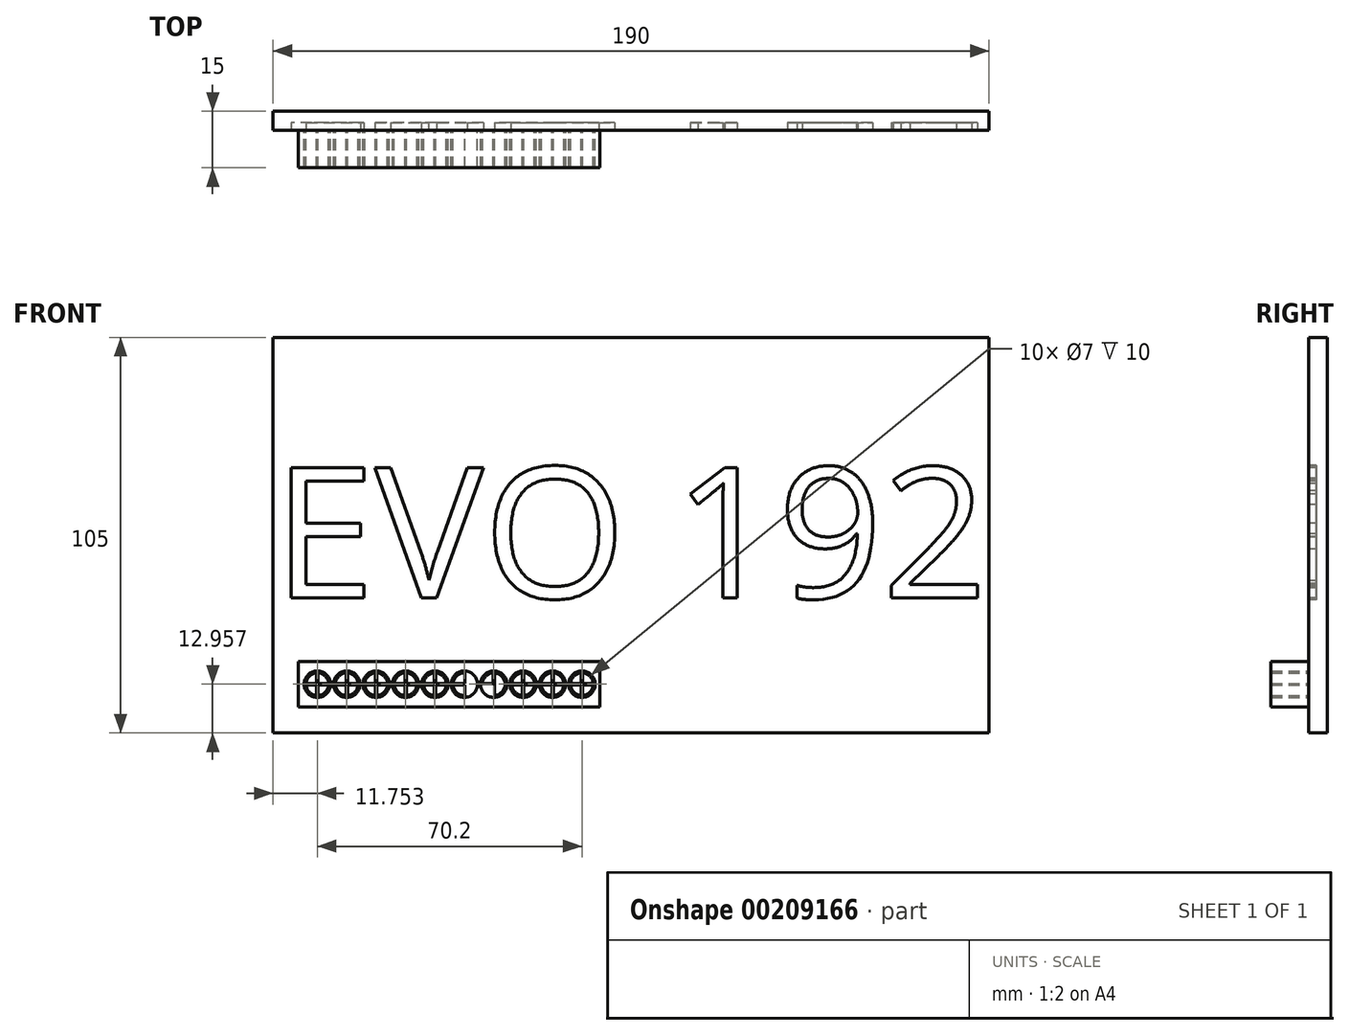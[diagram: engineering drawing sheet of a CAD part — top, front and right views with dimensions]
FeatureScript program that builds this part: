
annotation { "Feature Type Name" : "Feature", "Feature Type Description" : "" }
export const myFeature = defineFeature(function(context is Context, id is Id, definition is map)
    precondition{}
    {
        {
            var Q0;
            Q0=qCreatedBy(makeId("Front.planeOp"),FACE);
            var sketch = newSketch(context, id + "F0", { "sketchPlane" : qUnion([Q0])});
            skLineSegment(sketch, "E0.bottom", {"start": v(95, 52.5) * mm, "end": v(-95, 52.5) * mm});
            skLineSegment(sketch, "E0.top", {"start": v(95, -52.5) * mm, "end": v(-95, -52.5) * mm});
            skLineSegment(sketch, "E0.left", {"start": v(95, 52.5) * mm, "end": v(95, -52.5) * mm});
            skLineSegment(sketch, "E0.right", {"start": v(-95, 52.5) * mm, "end": v(-95, -52.5) * mm});
            skPoint(sketch, "E0.middle", {"position": v(0, 0) * mm});
            skSolve(sketch);
        }
        {
            var Q0;
            Q0 = qSketchRegion(id + "F0", true);
            extrude(context, id + "F1", {"entities" : qUnion([Q0]), "depth" : 5 * mm});
        }
        {
            var Q0;
            Q0=makeQuery(id+"F1.opExtrude","CAP_FACE",FACE,{"disambiguationData":[OSD([sQuery(id+"F0.wireOp",EDGE,"E0.bottom"),sQuery(id+"F0.wireOp",EDGE,"E0.top"),sQuery(id+"F0.wireOp",EDGE,"E0.left"),sQuery(id+"F0.wireOp",EDGE,"E0.right")])],"isStart":false});
            var sketch = newSketch(context, id + "F2", { "sketchPlane" : qUnion([Q0])});
            skText(sketch, "E1", { "text": "EVO 192", "fontName": "OpenSans-Regular.ttf"});
            const initialGuessF2  = {"E1": [-0.095, -0.01668, 1, 0, 0.03493]};
            skSetInitialGuess(sketch, initialGuessF2);
            skSolve(sketch);
        }
        {
            var Q0;
            Q0 = qSketchRegion(id + "F2", true);
            extrude(context, id + "F3", {"entities" : qUnion([Q0]), "operationType" : NewBodyOperationType.REMOVE, "oppositeDirection" : true, "depth" : 2 * mm});
        }
        {
            var Q0;
            {var subQ0=sQuery(id+"F0.wireOp",EDGE,"E0.top");var subQ1=sQuery(id+"F0.wireOp",EDGE,"E0.right");var subQ2=sQuery(id+"F0.wireOp",EDGE,"E0.bottom");var subQ3=sQuery(id+"F0.wireOp",EDGE,"E0.left");Q0=makeQuery(id+"F3.boolean.opBoolean","SPLIT",FACE,{"disambiguationData":[TD([makeQuery(id+"F1.opExtrude","SWEPT_FACE",FACE,{"disambiguationData":[OSD([subQ2])]})])],"derivedFrom":makeQuery(id+"F1.opExtrude","CAP_FACE",FACE,{"disambiguationData":[OSD([subQ2,subQ0,subQ3,subQ1])],"isStart":false})});}
            var sketch = newSketch(context, id + "F4", { "sketchPlane" : qUnion([Q0])});
            skLineSegment(sketch, "E2.bottom", {"start": v(-88.25, -33.54) * mm, "end": v(-8.25, -33.54) * mm});
            skLineSegment(sketch, "E2.top", {"start": v(-88.25, -45.54) * mm, "end": v(-8.25, -45.54) * mm});
            skLineSegment(sketch, "E2.left", {"start": v(-88.25, -33.54) * mm, "end": v(-88.25, -45.54) * mm});
            skLineSegment(sketch, "E2.right", {"start": v(-8.25, -33.54) * mm, "end": v(-8.25, -45.54) * mm});
            skCircle(sketch, "E3", {"center": v(-83.25, -39.54) * mm, "radius": 3 * mm});
            skLineSegment(sketch, "E4.0", {"start": v(-83.45, -36.54) * mm, "end": v(-83.45, -42.54) * mm});
            skLineSegment(sketch, "E5.0", {"start": v(-83.05, -36.54) * mm, "end": v(-83.05, -42.54) * mm});
            skLineSegment(sketch, "E6.0", {"start": v(-86.25, -39.74) * mm, "end": v(-80.25, -39.74) * mm});
            skLineSegment(sketch, "E7.0", {"start": v(-86.25, -39.34) * mm, "end": v(-80.25, -39.34) * mm});
            skCircle(sketch, "E8.1.0.0", {"center": v(-75.45, -39.54) * mm, "radius": 3 * mm});
            skLineSegment(sketch, "E8.1.0.1", {"start": v(-78.45, -39.34) * mm, "end": v(-72.45, -39.34) * mm});
            skLineSegment(sketch, "E8.1.0.2", {"start": v(-75.25, -36.54) * mm, "end": v(-75.25, -42.54) * mm});
            skLineSegment(sketch, "E8.1.0.3", {"start": v(-75.65, -36.54) * mm, "end": v(-75.65, -42.54) * mm});
            skLineSegment(sketch, "E8.1.0.4", {"start": v(-78.45, -39.74) * mm, "end": v(-72.45, -39.74) * mm});
            skCircle(sketch, "E8.2.0.0", {"center": v(-67.65, -39.54) * mm, "radius": 3 * mm});
            skLineSegment(sketch, "E8.2.0.1", {"start": v(-70.65, -39.34) * mm, "end": v(-64.65, -39.34) * mm});
            skLineSegment(sketch, "E8.2.0.2", {"start": v(-67.45, -36.54) * mm, "end": v(-67.45, -42.54) * mm});
            skLineSegment(sketch, "E8.2.0.3", {"start": v(-67.85, -36.54) * mm, "end": v(-67.85, -42.54) * mm});
            skLineSegment(sketch, "E8.2.0.4", {"start": v(-70.65, -39.74) * mm, "end": v(-64.65, -39.74) * mm});
            skCircle(sketch, "E8.3.0.0", {"center": v(-59.85, -39.54) * mm, "radius": 3 * mm});
            skLineSegment(sketch, "E8.3.0.1", {"start": v(-62.85, -39.34) * mm, "end": v(-56.85, -39.34) * mm});
            skLineSegment(sketch, "E8.3.0.2", {"start": v(-59.65, -36.54) * mm, "end": v(-59.65, -42.54) * mm});
            skLineSegment(sketch, "E8.3.0.3", {"start": v(-60.05, -36.54) * mm, "end": v(-60.05, -42.54) * mm});
            skLineSegment(sketch, "E8.3.0.4", {"start": v(-62.85, -39.74) * mm, "end": v(-56.85, -39.74) * mm});
            skCircle(sketch, "E8.4.0.0", {"center": v(-52.05, -39.54) * mm, "radius": 3 * mm});
            skLineSegment(sketch, "E8.4.0.1", {"start": v(-55.05, -39.34) * mm, "end": v(-49.05, -39.34) * mm});
            skLineSegment(sketch, "E8.4.0.2", {"start": v(-51.85, -36.54) * mm, "end": v(-51.85, -42.54) * mm});
            skLineSegment(sketch, "E8.4.0.3", {"start": v(-52.25, -36.54) * mm, "end": v(-52.25, -42.54) * mm});
            skLineSegment(sketch, "E8.4.0.4", {"start": v(-55.05, -39.74) * mm, "end": v(-49.05, -39.74) * mm});
            skCircle(sketch, "E8.5.0.0", {"center": v(-44.25, -39.54) * mm, "radius": 3 * mm});
            skLineSegment(sketch, "E8.5.0.1", {"start": v(-47.25, -39.34) * mm, "end": v(-41.25, -39.34) * mm});
            skLineSegment(sketch, "E8.5.0.2", {"start": v(-44.05, -36.54) * mm, "end": v(-44.05, -42.54) * mm});
            skLineSegment(sketch, "E8.5.0.3", {"start": v(-44.45, -36.54) * mm, "end": v(-44.45, -42.54) * mm});
            skLineSegment(sketch, "E8.5.0.4", {"start": v(-47.25, -39.74) * mm, "end": v(-41.25, -39.74) * mm});
            skCircle(sketch, "E8.6.0.0", {"center": v(-36.45, -39.54) * mm, "radius": 3 * mm});
            skLineSegment(sketch, "E8.6.0.1", {"start": v(-39.45, -39.34) * mm, "end": v(-33.45, -39.34) * mm});
            skLineSegment(sketch, "E8.6.0.2", {"start": v(-36.25, -36.54) * mm, "end": v(-36.25, -42.54) * mm});
            skLineSegment(sketch, "E8.6.0.3", {"start": v(-36.65, -36.54) * mm, "end": v(-36.65, -42.54) * mm});
            skLineSegment(sketch, "E8.6.0.4", {"start": v(-39.45, -39.74) * mm, "end": v(-33.45, -39.74) * mm});
            skCircle(sketch, "E8.7.0.0", {"center": v(-28.65, -39.54) * mm, "radius": 3 * mm});
            skLineSegment(sketch, "E8.7.0.1", {"start": v(-31.65, -39.34) * mm, "end": v(-25.65, -39.34) * mm});
            skLineSegment(sketch, "E8.7.0.2", {"start": v(-28.45, -36.54) * mm, "end": v(-28.45, -42.54) * mm});
            skLineSegment(sketch, "E8.7.0.3", {"start": v(-28.85, -36.54) * mm, "end": v(-28.85, -42.54) * mm});
            skLineSegment(sketch, "E8.7.0.4", {"start": v(-31.65, -39.74) * mm, "end": v(-25.65, -39.74) * mm});
            skCircle(sketch, "E8.8.0.0", {"center": v(-20.85, -39.54) * mm, "radius": 3 * mm});
            skLineSegment(sketch, "E8.8.0.1", {"start": v(-23.85, -39.34) * mm, "end": v(-17.85, -39.34) * mm});
            skLineSegment(sketch, "E8.8.0.2", {"start": v(-20.65, -36.54) * mm, "end": v(-20.65, -42.54) * mm});
            skLineSegment(sketch, "E8.8.0.3", {"start": v(-21.05, -36.54) * mm, "end": v(-21.05, -42.54) * mm});
            skLineSegment(sketch, "E8.8.0.4", {"start": v(-23.85, -39.74) * mm, "end": v(-17.85, -39.74) * mm});
            skCircle(sketch, "E8.9.0.0", {"center": v(-13.05, -39.54) * mm, "radius": 3 * mm});
            skLineSegment(sketch, "E8.9.0.1", {"start": v(-16.05, -39.34) * mm, "end": v(-10.05, -39.34) * mm});
            skLineSegment(sketch, "E8.9.0.2", {"start": v(-12.85, -36.54) * mm, "end": v(-12.85, -42.54) * mm});
            skLineSegment(sketch, "E8.9.0.3", {"start": v(-13.25, -36.54) * mm, "end": v(-13.25, -42.54) * mm});
            skLineSegment(sketch, "E8.9.0.4", {"start": v(-16.05, -39.74) * mm, "end": v(-10.05, -39.74) * mm});
            skLineSegment(sketch, "E8.direction1", {"start": v(-83.25, -39.54) * mm, "end": v(-75.45, -39.54) * mm, "construction": true});
            skCircle(sketch, "E9", {"center": v(-83.25, -39.54) * mm, "radius": 3.5 * mm});
            skCircle(sketch, "E10.1.0.0", {"center": v(-75.45, -39.54) * mm, "radius": 3.5 * mm});
            skCircle(sketch, "E10.2.0.0", {"center": v(-67.65, -39.54) * mm, "radius": 3.5 * mm});
            skCircle(sketch, "E10.3.0.0", {"center": v(-59.85, -39.54) * mm, "radius": 3.5 * mm});
            skCircle(sketch, "E10.4.0.0", {"center": v(-52.05, -39.54) * mm, "radius": 3.5 * mm});
            skCircle(sketch, "E10.5.0.0", {"center": v(-44.25, -39.54) * mm, "radius": 3.5 * mm});
            skCircle(sketch, "E10.6.0.0", {"center": v(-36.45, -39.54) * mm, "radius": 3.5 * mm});
            skCircle(sketch, "E10.7.0.0", {"center": v(-28.65, -39.54) * mm, "radius": 3.5 * mm});
            skCircle(sketch, "E10.8.0.0", {"center": v(-20.85, -39.54) * mm, "radius": 3.5 * mm});
            skCircle(sketch, "E10.9.0.0", {"center": v(-13.05, -39.54) * mm, "radius": 3.5 * mm});
            skSolve(sketch);
        }
        {
            var Q0;
            Q0 = qSketchRegion(id + "F4", true);
            var Q1;
            {var subQ0=sQuery(id+"F4.wireOp",EDGE,"E4.0");var subQ1=sQuery(id+"F4.wireOp",EDGE,"E3");var subQ2=makeQuery(id+"F4.imprint","INTERSECT",VERTEX,{"disambiguationData":[OD(0.0)],"derivedFrom":[subQ1,subQ0]});Q1=makeQuery(id+"F4.imprint","IMPRINT",FACE,{"disambiguationData":[TD([[makeQuery(id+"F4.imprint","IMPRINT",EDGE,{"disambiguationData":[TD([[subQ2,-1.0]])],"derivedFrom":subQ1}),1.0]])]});}
            var Q2;
            {var subQ0=sQuery(id+"F4.wireOp",EDGE,"E5.0");var subQ1=sQuery(id+"F4.wireOp",EDGE,"E3");var subQ2=makeQuery(id+"F4.imprint","INTERSECT",VERTEX,{"disambiguationData":[OD(0.0)],"derivedFrom":[subQ1,subQ0]});Q2=makeQuery(id+"F4.imprint","IMPRINT",FACE,{"disambiguationData":[TD([[makeQuery(id+"F4.imprint","IMPRINT",EDGE,{"disambiguationData":[TD([[subQ2,1.0]])],"derivedFrom":subQ1}),1.0]])]});}
            var Q3;
            {var subQ0=sQuery(id+"F4.wireOp",EDGE,"E5.0");var subQ1=sQuery(id+"F4.wireOp",EDGE,"E3");var subQ2=makeQuery(id+"F4.imprint","INTERSECT",VERTEX,{"disambiguationData":[OD(1.0)],"derivedFrom":[subQ1,subQ0]});Q3=makeQuery(id+"F4.imprint","IMPRINT",FACE,{"disambiguationData":[TD([[makeQuery(id+"F4.imprint","IMPRINT",EDGE,{"disambiguationData":[TD([[subQ2,-1.0]])],"derivedFrom":subQ1}),1.0]])]});}
            var Q4;
            {var subQ0=sQuery(id+"F4.wireOp",EDGE,"E6.0");var subQ1=sQuery(id+"F4.wireOp",EDGE,"E3");var subQ2=makeQuery(id+"F4.imprint","INTERSECT",VERTEX,{"disambiguationData":[OD(0.0)],"derivedFrom":[subQ1,subQ0]});Q4=makeQuery(id+"F4.imprint","IMPRINT",FACE,{"disambiguationData":[TD([[makeQuery(id+"F4.imprint","IMPRINT",EDGE,{"disambiguationData":[TD([[subQ2,-1.0]])],"derivedFrom":subQ1}),1.0]])]});}
            var Q5;
            {var subQ0=sQuery(id+"F4.wireOp",EDGE,"E8.1.0.3");var subQ1=sQuery(id+"F4.wireOp",EDGE,"E8.1.0.0");var subQ2=makeQuery(id+"F4.imprint","INTERSECT",VERTEX,{"disambiguationData":[OD(0.0)],"derivedFrom":[subQ1,subQ0]});Q5=makeQuery(id+"F4.imprint","IMPRINT",FACE,{"disambiguationData":[TD([[makeQuery(id+"F4.imprint","IMPRINT",EDGE,{"disambiguationData":[TD([[subQ2,-1.0]])],"derivedFrom":subQ1}),1.0]])]});}
            var Q6;
            {var subQ0=sQuery(id+"F4.wireOp",EDGE,"E8.1.0.2");var subQ1=sQuery(id+"F4.wireOp",EDGE,"E8.1.0.0");var subQ2=makeQuery(id+"F4.imprint","INTERSECT",VERTEX,{"disambiguationData":[OD(0.0)],"derivedFrom":[subQ1,subQ0]});Q6=makeQuery(id+"F4.imprint","IMPRINT",FACE,{"disambiguationData":[TD([[makeQuery(id+"F4.imprint","IMPRINT",EDGE,{"disambiguationData":[TD([[subQ2,1.0]])],"derivedFrom":subQ1}),1.0]])]});}
            var Q7;
            {var subQ0=sQuery(id+"F4.wireOp",EDGE,"E8.1.0.2");var subQ1=sQuery(id+"F4.wireOp",EDGE,"E8.1.0.0");var subQ2=makeQuery(id+"F4.imprint","INTERSECT",VERTEX,{"disambiguationData":[OD(1.0)],"derivedFrom":[subQ1,subQ0]});Q7=makeQuery(id+"F4.imprint","IMPRINT",FACE,{"disambiguationData":[TD([[makeQuery(id+"F4.imprint","IMPRINT",EDGE,{"disambiguationData":[TD([[subQ2,-1.0]])],"derivedFrom":subQ1}),1.0]])]});}
            var Q8;
            {var subQ0=sQuery(id+"F4.wireOp",EDGE,"E8.1.0.4");var subQ1=sQuery(id+"F4.wireOp",EDGE,"E8.1.0.0");var subQ2=makeQuery(id+"F4.imprint","INTERSECT",VERTEX,{"disambiguationData":[OD(0.0)],"derivedFrom":[subQ1,subQ0]});Q8=makeQuery(id+"F4.imprint","IMPRINT",FACE,{"disambiguationData":[TD([[makeQuery(id+"F4.imprint","IMPRINT",EDGE,{"disambiguationData":[TD([[subQ2,-1.0]])],"derivedFrom":subQ1}),1.0]])]});}
            var Q9;
            {var subQ0=sQuery(id+"F4.wireOp",EDGE,"E8.2.0.3");var subQ1=sQuery(id+"F4.wireOp",EDGE,"E8.2.0.0");var subQ2=makeQuery(id+"F4.imprint","INTERSECT",VERTEX,{"disambiguationData":[OD(0.0)],"derivedFrom":[subQ1,subQ0]});Q9=makeQuery(id+"F4.imprint","IMPRINT",FACE,{"disambiguationData":[TD([[makeQuery(id+"F4.imprint","IMPRINT",EDGE,{"disambiguationData":[TD([[subQ2,-1.0]])],"derivedFrom":subQ1}),1.0]])]});}
            var Q10;
            {var subQ0=sQuery(id+"F4.wireOp",EDGE,"E8.2.0.2");var subQ1=sQuery(id+"F4.wireOp",EDGE,"E8.2.0.0");var subQ2=makeQuery(id+"F4.imprint","INTERSECT",VERTEX,{"disambiguationData":[OD(0.0)],"derivedFrom":[subQ1,subQ0]});Q10=makeQuery(id+"F4.imprint","IMPRINT",FACE,{"disambiguationData":[TD([[makeQuery(id+"F4.imprint","IMPRINT",EDGE,{"disambiguationData":[TD([[subQ2,1.0]])],"derivedFrom":subQ1}),1.0]])]});}
            var Q11;
            {var subQ0=sQuery(id+"F4.wireOp",EDGE,"E8.2.0.2");var subQ1=sQuery(id+"F4.wireOp",EDGE,"E8.2.0.0");var subQ2=makeQuery(id+"F4.imprint","INTERSECT",VERTEX,{"disambiguationData":[OD(1.0)],"derivedFrom":[subQ1,subQ0]});Q11=makeQuery(id+"F4.imprint","IMPRINT",FACE,{"disambiguationData":[TD([[makeQuery(id+"F4.imprint","IMPRINT",EDGE,{"disambiguationData":[TD([[subQ2,-1.0]])],"derivedFrom":subQ1}),1.0]])]});}
            var Q12;
            {var subQ0=sQuery(id+"F4.wireOp",EDGE,"E8.2.0.4");var subQ1=sQuery(id+"F4.wireOp",EDGE,"E8.2.0.0");var subQ2=makeQuery(id+"F4.imprint","INTERSECT",VERTEX,{"disambiguationData":[OD(0.0)],"derivedFrom":[subQ1,subQ0]});Q12=makeQuery(id+"F4.imprint","IMPRINT",FACE,{"disambiguationData":[TD([[makeQuery(id+"F4.imprint","IMPRINT",EDGE,{"disambiguationData":[TD([[subQ2,-1.0]])],"derivedFrom":subQ1}),1.0]])]});}
            var Q13;
            {var subQ0=sQuery(id+"F4.wireOp",EDGE,"E8.3.0.3");var subQ1=sQuery(id+"F4.wireOp",EDGE,"E8.3.0.0");var subQ2=makeQuery(id+"F4.imprint","INTERSECT",VERTEX,{"disambiguationData":[OD(0.0)],"derivedFrom":[subQ1,subQ0]});Q13=makeQuery(id+"F4.imprint","IMPRINT",FACE,{"disambiguationData":[TD([[makeQuery(id+"F4.imprint","IMPRINT",EDGE,{"disambiguationData":[TD([[subQ2,-1.0]])],"derivedFrom":subQ1}),1.0]])]});}
            var Q14;
            {var subQ0=sQuery(id+"F4.wireOp",EDGE,"E8.3.0.2");var subQ1=sQuery(id+"F4.wireOp",EDGE,"E8.3.0.0");var subQ2=makeQuery(id+"F4.imprint","INTERSECT",VERTEX,{"disambiguationData":[OD(0.0)],"derivedFrom":[subQ1,subQ0]});Q14=makeQuery(id+"F4.imprint","IMPRINT",FACE,{"disambiguationData":[TD([[makeQuery(id+"F4.imprint","IMPRINT",EDGE,{"disambiguationData":[TD([[subQ2,1.0]])],"derivedFrom":subQ1}),1.0]])]});}
            var Q15;
            {var subQ0=sQuery(id+"F4.wireOp",EDGE,"E8.3.0.2");var subQ1=sQuery(id+"F4.wireOp",EDGE,"E8.3.0.0");var subQ2=makeQuery(id+"F4.imprint","INTERSECT",VERTEX,{"disambiguationData":[OD(1.0)],"derivedFrom":[subQ1,subQ0]});Q15=makeQuery(id+"F4.imprint","IMPRINT",FACE,{"disambiguationData":[TD([[makeQuery(id+"F4.imprint","IMPRINT",EDGE,{"disambiguationData":[TD([[subQ2,-1.0]])],"derivedFrom":subQ1}),1.0]])]});}
            var Q16;
            {var subQ0=sQuery(id+"F4.wireOp",EDGE,"E8.3.0.4");var subQ1=sQuery(id+"F4.wireOp",EDGE,"E8.3.0.0");var subQ2=makeQuery(id+"F4.imprint","INTERSECT",VERTEX,{"disambiguationData":[OD(0.0)],"derivedFrom":[subQ1,subQ0]});Q16=makeQuery(id+"F4.imprint","IMPRINT",FACE,{"disambiguationData":[TD([[makeQuery(id+"F4.imprint","IMPRINT",EDGE,{"disambiguationData":[TD([[subQ2,-1.0]])],"derivedFrom":subQ1}),1.0]])]});}
            var Q17;
            {var subQ0=sQuery(id+"F4.wireOp",EDGE,"E8.4.0.3");var subQ1=sQuery(id+"F4.wireOp",EDGE,"E8.4.0.0");var subQ2=makeQuery(id+"F4.imprint","INTERSECT",VERTEX,{"disambiguationData":[OD(0.0)],"derivedFrom":[subQ1,subQ0]});Q17=makeQuery(id+"F4.imprint","IMPRINT",FACE,{"disambiguationData":[TD([[makeQuery(id+"F4.imprint","IMPRINT",EDGE,{"disambiguationData":[TD([[subQ2,-1.0]])],"derivedFrom":subQ1}),1.0]])]});}
            var Q18;
            {var subQ0=sQuery(id+"F4.wireOp",EDGE,"E8.4.0.2");var subQ1=sQuery(id+"F4.wireOp",EDGE,"E8.4.0.0");var subQ2=makeQuery(id+"F4.imprint","INTERSECT",VERTEX,{"disambiguationData":[OD(0.0)],"derivedFrom":[subQ1,subQ0]});Q18=makeQuery(id+"F4.imprint","IMPRINT",FACE,{"disambiguationData":[TD([[makeQuery(id+"F4.imprint","IMPRINT",EDGE,{"disambiguationData":[TD([[subQ2,1.0]])],"derivedFrom":subQ1}),1.0]])]});}
            var Q19;
            {var subQ0=sQuery(id+"F4.wireOp",EDGE,"E8.4.0.2");var subQ1=sQuery(id+"F4.wireOp",EDGE,"E8.4.0.0");var subQ2=makeQuery(id+"F4.imprint","INTERSECT",VERTEX,{"disambiguationData":[OD(1.0)],"derivedFrom":[subQ1,subQ0]});Q19=makeQuery(id+"F4.imprint","IMPRINT",FACE,{"disambiguationData":[TD([[makeQuery(id+"F4.imprint","IMPRINT",EDGE,{"disambiguationData":[TD([[subQ2,-1.0]])],"derivedFrom":subQ1}),1.0]])]});}
            var Q20;
            {var subQ0=sQuery(id+"F4.wireOp",EDGE,"E8.4.0.4");var subQ1=sQuery(id+"F4.wireOp",EDGE,"E8.4.0.0");var subQ2=makeQuery(id+"F4.imprint","INTERSECT",VERTEX,{"disambiguationData":[OD(0.0)],"derivedFrom":[subQ1,subQ0]});Q20=makeQuery(id+"F4.imprint","IMPRINT",FACE,{"disambiguationData":[TD([[makeQuery(id+"F4.imprint","IMPRINT",EDGE,{"disambiguationData":[TD([[subQ2,-1.0]])],"derivedFrom":subQ1}),1.0]])]});}
            var Q21;
            {var subQ0=sQuery(id+"F4.wireOp",EDGE,"E8.5.0.3");var subQ1=sQuery(id+"F4.wireOp",EDGE,"E8.5.0.0");var subQ2=makeQuery(id+"F4.imprint","INTERSECT",VERTEX,{"disambiguationData":[OD(0.0)],"derivedFrom":[subQ1,subQ0]});Q21=makeQuery(id+"F4.imprint","IMPRINT",FACE,{"disambiguationData":[TD([[makeQuery(id+"F4.imprint","IMPRINT",EDGE,{"disambiguationData":[TD([[subQ2,-1.0]])],"derivedFrom":subQ1}),1.0]])]});}
            var Q22;
            {var subQ0=sQuery(id+"F4.wireOp",EDGE,"E8.5.0.2");var subQ1=sQuery(id+"F4.wireOp",EDGE,"E8.5.0.0");var subQ2=makeQuery(id+"F4.imprint","INTERSECT",VERTEX,{"disambiguationData":[OD(0.0)],"derivedFrom":[subQ1,subQ0]});Q22=makeQuery(id+"F4.imprint","IMPRINT",FACE,{"disambiguationData":[TD([[makeQuery(id+"F4.imprint","IMPRINT",EDGE,{"disambiguationData":[TD([[subQ2,1.0]])],"derivedFrom":subQ1}),1.0]])]});}
            var Q23;
            {var subQ0=sQuery(id+"F4.wireOp",EDGE,"E8.5.0.2");var subQ1=sQuery(id+"F4.wireOp",EDGE,"E8.5.0.0");var subQ2=makeQuery(id+"F4.imprint","INTERSECT",VERTEX,{"disambiguationData":[OD(1.0)],"derivedFrom":[subQ1,subQ0]});Q23=makeQuery(id+"F4.imprint","IMPRINT",FACE,{"disambiguationData":[TD([[makeQuery(id+"F4.imprint","IMPRINT",EDGE,{"disambiguationData":[TD([[subQ2,-1.0]])],"derivedFrom":subQ1}),1.0]])]});}
            var Q24;
            {var subQ0=sQuery(id+"F4.wireOp",EDGE,"E8.5.0.4");var subQ1=sQuery(id+"F4.wireOp",EDGE,"E8.5.0.0");var subQ2=makeQuery(id+"F4.imprint","INTERSECT",VERTEX,{"disambiguationData":[OD(0.0)],"derivedFrom":[subQ1,subQ0]});Q24=makeQuery(id+"F4.imprint","IMPRINT",FACE,{"disambiguationData":[TD([[makeQuery(id+"F4.imprint","IMPRINT",EDGE,{"disambiguationData":[TD([[subQ2,-1.0]])],"derivedFrom":subQ1}),1.0]])]});}
            var Q25;
            {var subQ0=sQuery(id+"F4.wireOp",EDGE,"E8.6.0.2");var subQ1=sQuery(id+"F4.wireOp",EDGE,"E8.6.0.0");var subQ2=makeQuery(id+"F4.imprint","INTERSECT",VERTEX,{"disambiguationData":[OD(0.0)],"derivedFrom":[subQ1,subQ0]});Q25=makeQuery(id+"F4.imprint","IMPRINT",FACE,{"disambiguationData":[TD([[makeQuery(id+"F4.imprint","IMPRINT",EDGE,{"disambiguationData":[TD([[subQ2,1.0]])],"derivedFrom":subQ1}),1.0]])]});}
            var Q26;
            {var subQ0=sQuery(id+"F4.wireOp",EDGE,"E8.6.0.3");var subQ1=sQuery(id+"F4.wireOp",EDGE,"E8.6.0.0");var subQ2=makeQuery(id+"F4.imprint","INTERSECT",VERTEX,{"disambiguationData":[OD(0.0)],"derivedFrom":[subQ1,subQ0]});Q26=makeQuery(id+"F4.imprint","IMPRINT",FACE,{"disambiguationData":[TD([[makeQuery(id+"F4.imprint","IMPRINT",EDGE,{"disambiguationData":[TD([[subQ2,-1.0]])],"derivedFrom":subQ1}),1.0]])]});}
            var Q27;
            {var subQ0=sQuery(id+"F4.wireOp",EDGE,"E8.6.0.4");var subQ1=sQuery(id+"F4.wireOp",EDGE,"E8.6.0.0");var subQ2=makeQuery(id+"F4.imprint","INTERSECT",VERTEX,{"disambiguationData":[OD(0.0)],"derivedFrom":[subQ1,subQ0]});Q27=makeQuery(id+"F4.imprint","IMPRINT",FACE,{"disambiguationData":[TD([[makeQuery(id+"F4.imprint","IMPRINT",EDGE,{"disambiguationData":[TD([[subQ2,-1.0]])],"derivedFrom":subQ1}),1.0]])]});}
            var Q28;
            {var subQ0=sQuery(id+"F4.wireOp",EDGE,"E8.6.0.2");var subQ1=sQuery(id+"F4.wireOp",EDGE,"E8.6.0.0");var subQ2=makeQuery(id+"F4.imprint","INTERSECT",VERTEX,{"disambiguationData":[OD(1.0)],"derivedFrom":[subQ1,subQ0]});Q28=makeQuery(id+"F4.imprint","IMPRINT",FACE,{"disambiguationData":[TD([[makeQuery(id+"F4.imprint","IMPRINT",EDGE,{"disambiguationData":[TD([[subQ2,-1.0]])],"derivedFrom":subQ1}),1.0]])]});}
            var Q29;
            {var subQ0=sQuery(id+"F4.wireOp",EDGE,"E8.7.0.3");var subQ1=sQuery(id+"F4.wireOp",EDGE,"E8.7.0.0");var subQ2=makeQuery(id+"F4.imprint","INTERSECT",VERTEX,{"disambiguationData":[OD(0.0)],"derivedFrom":[subQ1,subQ0]});Q29=makeQuery(id+"F4.imprint","IMPRINT",FACE,{"disambiguationData":[TD([[makeQuery(id+"F4.imprint","IMPRINT",EDGE,{"disambiguationData":[TD([[subQ2,-1.0]])],"derivedFrom":subQ1}),1.0]])]});}
            var Q30;
            {var subQ0=sQuery(id+"F4.wireOp",EDGE,"E8.7.0.2");var subQ1=sQuery(id+"F4.wireOp",EDGE,"E8.7.0.0");var subQ2=makeQuery(id+"F4.imprint","INTERSECT",VERTEX,{"disambiguationData":[OD(0.0)],"derivedFrom":[subQ1,subQ0]});Q30=makeQuery(id+"F4.imprint","IMPRINT",FACE,{"disambiguationData":[TD([[makeQuery(id+"F4.imprint","IMPRINT",EDGE,{"disambiguationData":[TD([[subQ2,1.0]])],"derivedFrom":subQ1}),1.0]])]});}
            var Q31;
            {var subQ0=sQuery(id+"F4.wireOp",EDGE,"E8.7.0.2");var subQ1=sQuery(id+"F4.wireOp",EDGE,"E8.7.0.0");var subQ2=makeQuery(id+"F4.imprint","INTERSECT",VERTEX,{"disambiguationData":[OD(1.0)],"derivedFrom":[subQ1,subQ0]});Q31=makeQuery(id+"F4.imprint","IMPRINT",FACE,{"disambiguationData":[TD([[makeQuery(id+"F4.imprint","IMPRINT",EDGE,{"disambiguationData":[TD([[subQ2,-1.0]])],"derivedFrom":subQ1}),1.0]])]});}
            var Q32;
            {var subQ0=sQuery(id+"F4.wireOp",EDGE,"E8.7.0.4");var subQ1=sQuery(id+"F4.wireOp",EDGE,"E8.7.0.0");var subQ2=makeQuery(id+"F4.imprint","INTERSECT",VERTEX,{"disambiguationData":[OD(0.0)],"derivedFrom":[subQ1,subQ0]});Q32=makeQuery(id+"F4.imprint","IMPRINT",FACE,{"disambiguationData":[TD([[makeQuery(id+"F4.imprint","IMPRINT",EDGE,{"disambiguationData":[TD([[subQ2,-1.0]])],"derivedFrom":subQ1}),1.0]])]});}
            var Q33;
            {var subQ0=sQuery(id+"F4.wireOp",EDGE,"E8.8.0.3");var subQ1=sQuery(id+"F4.wireOp",EDGE,"E8.8.0.0");var subQ2=makeQuery(id+"F4.imprint","INTERSECT",VERTEX,{"disambiguationData":[OD(0.0)],"derivedFrom":[subQ1,subQ0]});Q33=makeQuery(id+"F4.imprint","IMPRINT",FACE,{"disambiguationData":[TD([[makeQuery(id+"F4.imprint","IMPRINT",EDGE,{"disambiguationData":[TD([[subQ2,-1.0]])],"derivedFrom":subQ1}),1.0]])]});}
            var Q34;
            {var subQ0=sQuery(id+"F4.wireOp",EDGE,"E8.8.0.2");var subQ1=sQuery(id+"F4.wireOp",EDGE,"E8.8.0.0");var subQ2=makeQuery(id+"F4.imprint","INTERSECT",VERTEX,{"disambiguationData":[OD(0.0)],"derivedFrom":[subQ1,subQ0]});Q34=makeQuery(id+"F4.imprint","IMPRINT",FACE,{"disambiguationData":[TD([[makeQuery(id+"F4.imprint","IMPRINT",EDGE,{"disambiguationData":[TD([[subQ2,1.0]])],"derivedFrom":subQ1}),1.0]])]});}
            var Q35;
            {var subQ0=sQuery(id+"F4.wireOp",EDGE,"E8.8.0.2");var subQ1=sQuery(id+"F4.wireOp",EDGE,"E8.8.0.0");var subQ2=makeQuery(id+"F4.imprint","INTERSECT",VERTEX,{"disambiguationData":[OD(1.0)],"derivedFrom":[subQ1,subQ0]});Q35=makeQuery(id+"F4.imprint","IMPRINT",FACE,{"disambiguationData":[TD([[makeQuery(id+"F4.imprint","IMPRINT",EDGE,{"disambiguationData":[TD([[subQ2,-1.0]])],"derivedFrom":subQ1}),1.0]])]});}
            var Q36;
            {var subQ0=sQuery(id+"F4.wireOp",EDGE,"E8.8.0.4");var subQ1=sQuery(id+"F4.wireOp",EDGE,"E8.8.0.0");var subQ2=makeQuery(id+"F4.imprint","INTERSECT",VERTEX,{"disambiguationData":[OD(0.0)],"derivedFrom":[subQ1,subQ0]});Q36=makeQuery(id+"F4.imprint","IMPRINT",FACE,{"disambiguationData":[TD([[makeQuery(id+"F4.imprint","IMPRINT",EDGE,{"disambiguationData":[TD([[subQ2,-1.0]])],"derivedFrom":subQ1}),1.0]])]});}
            var Q37;
            {var subQ0=sQuery(id+"F4.wireOp",EDGE,"E8.9.0.3");var subQ1=sQuery(id+"F4.wireOp",EDGE,"E8.9.0.0");var subQ2=makeQuery(id+"F4.imprint","INTERSECT",VERTEX,{"disambiguationData":[OD(0.0)],"derivedFrom":[subQ1,subQ0]});Q37=makeQuery(id+"F4.imprint","IMPRINT",FACE,{"disambiguationData":[TD([[makeQuery(id+"F4.imprint","IMPRINT",EDGE,{"disambiguationData":[TD([[subQ2,-1.0]])],"derivedFrom":subQ1}),1.0]])]});}
            var Q38;
            {var subQ0=sQuery(id+"F4.wireOp",EDGE,"E8.9.0.2");var subQ1=sQuery(id+"F4.wireOp",EDGE,"E8.9.0.0");var subQ2=makeQuery(id+"F4.imprint","INTERSECT",VERTEX,{"disambiguationData":[OD(0.0)],"derivedFrom":[subQ1,subQ0]});Q38=makeQuery(id+"F4.imprint","IMPRINT",FACE,{"disambiguationData":[TD([[makeQuery(id+"F4.imprint","IMPRINT",EDGE,{"disambiguationData":[TD([[subQ2,1.0]])],"derivedFrom":subQ1}),1.0]])]});}
            var Q39;
            {var subQ0=sQuery(id+"F4.wireOp",EDGE,"E8.9.0.2");var subQ1=sQuery(id+"F4.wireOp",EDGE,"E8.9.0.0");var subQ2=makeQuery(id+"F4.imprint","INTERSECT",VERTEX,{"disambiguationData":[OD(1.0)],"derivedFrom":[subQ1,subQ0]});Q39=makeQuery(id+"F4.imprint","IMPRINT",FACE,{"disambiguationData":[TD([[makeQuery(id+"F4.imprint","IMPRINT",EDGE,{"disambiguationData":[TD([[subQ2,-1.0]])],"derivedFrom":subQ1}),1.0]])]});}
            var Q40;
            {var subQ0=sQuery(id+"F4.wireOp",EDGE,"E8.9.0.4");var subQ1=sQuery(id+"F4.wireOp",EDGE,"E8.9.0.0");var subQ2=makeQuery(id+"F4.imprint","INTERSECT",VERTEX,{"disambiguationData":[OD(0.0)],"derivedFrom":[subQ1,subQ0]});Q40=makeQuery(id+"F4.imprint","IMPRINT",FACE,{"disambiguationData":[TD([[makeQuery(id+"F4.imprint","IMPRINT",EDGE,{"disambiguationData":[TD([[subQ2,-1.0]])],"derivedFrom":subQ1}),1.0]])]});}
            extrude(context, id + "F5", {"entities" : qUnion([Q0, Q1, Q2, Q3, Q4, Q5, Q6, Q7, Q8, Q9, Q10, Q11, Q12, Q13, Q14, Q15, Q16, Q17, Q18, Q19, Q20, Q21, Q22, Q23, Q24, Q25, Q26, Q27, Q28, Q29, Q30, Q31, Q32, Q33, Q34, Q35, Q36, Q37, Q38, Q39, Q40]), "operationType" : NewBodyOperationType.ADD, "depth" : 10 * mm});
        }
    });
